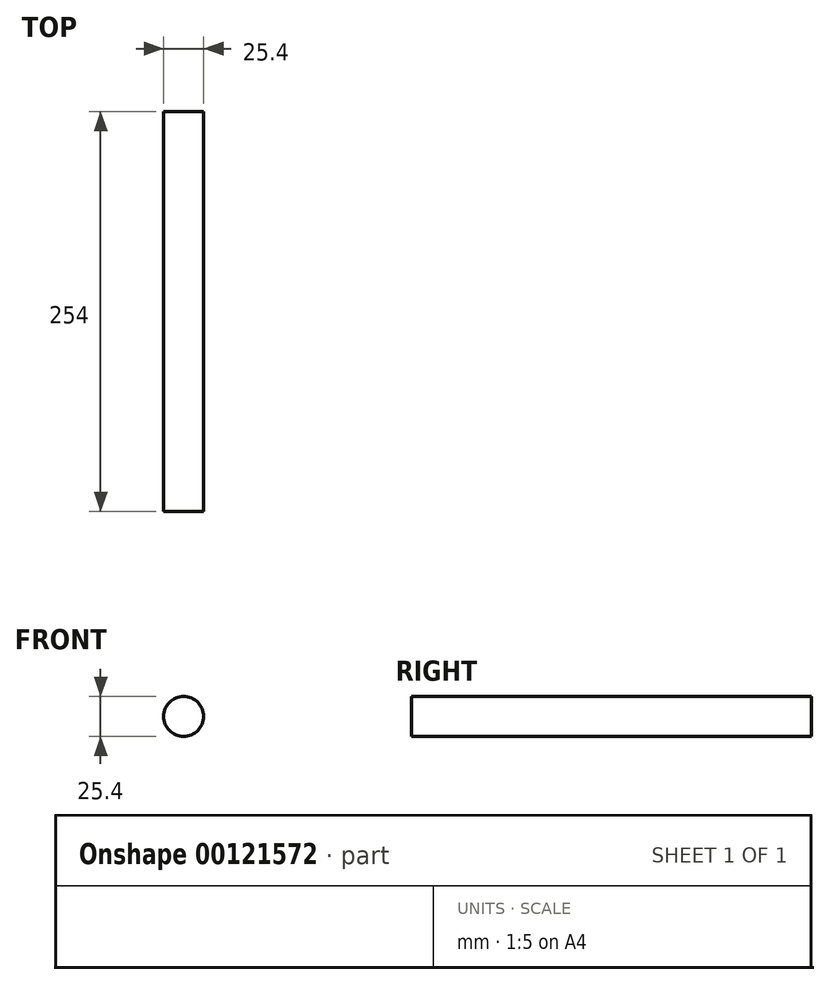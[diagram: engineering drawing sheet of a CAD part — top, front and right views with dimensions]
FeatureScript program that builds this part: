
annotation { "Feature Type Name" : "Feature", "Feature Type Description" : "" }
export const myFeature = defineFeature(function(context is Context, id is Id, definition is map)
    precondition{}
    {
        {
            var Q0;
            Q0=qCreatedBy(makeId("Front.planeOp"),FACE);
            var sketch = newSketch(context, id + "F0", { "sketchPlane" : qUnion([Q0])});
            skCircle(sketch, "E0", {"center": v(0, 0) * mm, "radius": 12.7 * mm});
            skCircle(sketch, "E1", {"center": v(0, 0) * mm, "radius": 38.1 * mm});
            skSolve(sketch);
        }
        {
            var Q0;
            Q0=makeQuery(id+"F0.imprint","IMPRINT",FACE,{"disambiguationData":[TD([[makeQuery(id+"F0.imprint","IMPRINT",EDGE,{"derivedFrom":sQuery(id+"F0.wireOp",EDGE,"E0")}),1.0]])]});
            extrude(context, id + "F1", {"entities" : qUnion([Q0]), "depth" : 254 * mm});
        }
    });
